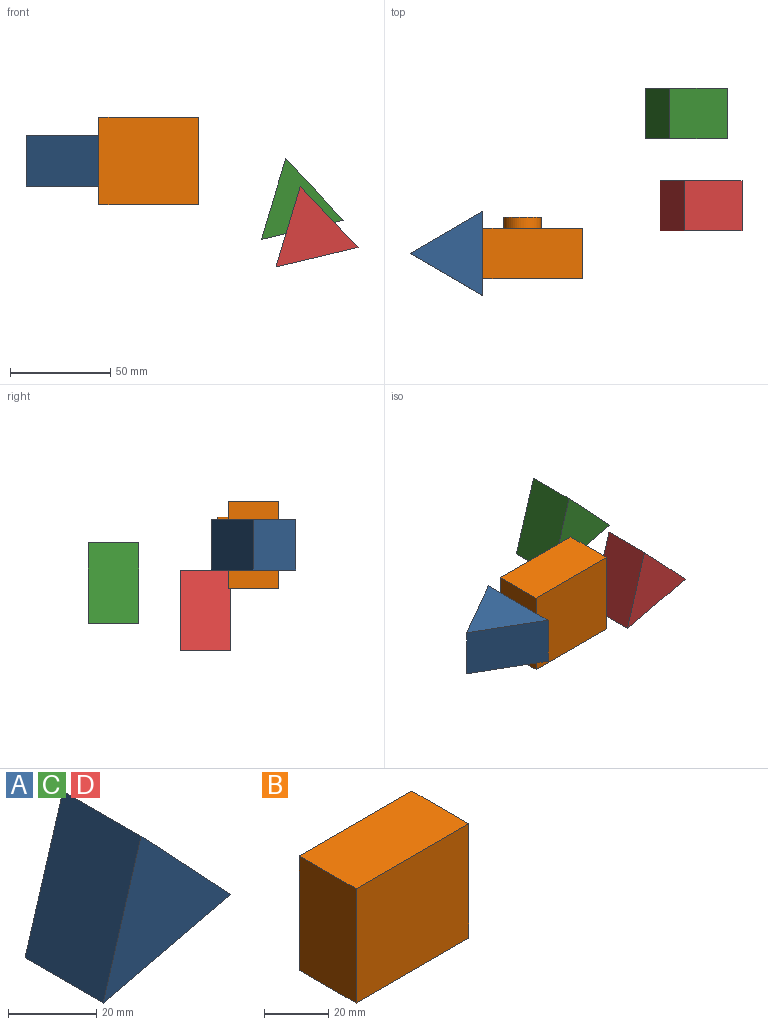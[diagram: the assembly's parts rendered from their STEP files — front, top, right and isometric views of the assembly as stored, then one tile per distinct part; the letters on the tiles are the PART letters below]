
ASSEMBLY  parts=4 mates=1
PART A: 5 faces, bbox 40.8x25x40.2 mm
  f0: plane 40.82x25mm, normal (0.23,0,-0.97), area 1048.6mm2, adj f1,f2,f3,f4
  f1: plane 30.54x28.76mm, normal (0.73,0,0.69), area 1048.6mm2, adj f0,f2,f3,f4
  f2: plane 40.17x25mm, normal (-0.96,0,0.29), area 1048.6mm2, adj f0,f1,f3,f4
  f3: plane 40.82x40.17mm, normal (0,-1,0), area 761.9mm2, adj f0,f1,f2
  f4: plane 40.82x40.17mm, normal (0,1,0), area 761.9mm2, adj f0,f1,f2
PART B: 12 faces, bbox 49.6x30.6x43.6 mm
  f0: plane 49.55x25mm, normal (0,0,1), area 1238.9mm2, adj f1,f3,f4,f5
  f1: plane 43.57x25mm, normal (-1,0,0), area 1089.3mm2, adj f0,f2,f4,f5
  f2: plane 49.55x25mm, normal (0,0,-1), area 1136.9mm2, adj f1,f3,f4,f5,f10
  f3: plane 43.57x25mm, normal (1,0,0), area 1089.3mm2, adj f0,f2,f4,f5
  f4: plane 49.55x43.57mm, normal (0,-1,0), area 2159.3mm2, adj f0,f1,f2,f3
  f5: plane 49.55x43.57mm, normal (0,1,0), area 1884.6mm2, adj f0,f1,f2,f3,f7
  f6: cylinder r=8.22mm len=16.44mm, axis (0,-1,0), area 289.2mm2, adj f8,f9
  f7: cylinder r=9.35mm len=18.7mm, axis (0,-1,0), area 329mm2, adj f5,f8
  f8: plane 18.7x18.7mm, normal (0,1,0), area 62.4mm2, adj f6,f7
  f9: plane 16.44x16.44mm, normal (0,1,0), area 212.3mm2, adj f6
  f10: cylinder r=5.7mm len=25mm, axis (0,0,-1), area 894.9mm2, adj f2,f11
  f11: plane 11.39x11.39mm, normal (0,0,-1), area 102mm2, adj f10
PART C: same geometry as A
PART D: same geometry as A
PLACE A rot(axis=(0.87,0.35,0.35),97.8deg) t=(-6.04,-55.27,26.96)mm
PLACE B t=(-6.91,-9.72,4.99)mm
PLACE C t=(67.32,59.96,52.87)mm
PLACE D t=(74.58,14.11,39.23)mm
MATE fastened A.f1 <-> B.f1  axis (1,0,0) through (-47.72,-22.22,14.46)mm
